# Revit family: Toilet-Round-American_Standard-Colony-221DB_Series
name_source: partatom
category: Plumbing Fixtures
units: mm (PartAtom-declared; Revit-internal decimal feet)

## family parameters
Always vertical = No
Cut with Voids When Loaded = No
OmniClass Number = 23.45.05.21.11.11
OmniClass Title = Water Operated Water Closets
Part Type = Normal
Room Calculation Point = No
Round Connector Dimension = Use Radius
Shared = Yes
Work Plane-Based = Yes

## types (3) — shared parameters
3251D.101 - Round Front Bowl = Yes
4192B.104 - Tank complete with trip lever located on left side = Yes
4192B.105 - Tank complete with trip lever located on right side = No
5322.011 - Rise and Shine solid plastic closed front round seat with cover = No
Assembly Code = D2010110
Bowl Shape = Round
CW Connection = Yes
CWFU = 5
Cold Water Connection Diameter = 3/8"
Cold Water Connection Height = 10"
Cold Water Connection Radius = 3/16"
Cold Water Connection Width = 6"
Default Elevation = 0"
Description = Colony® Two-Piece 1.28 gpf/4.8 Lpf Standard Height Round Front 10-Inch Rough Toilet Less Seat
Flush Rate = 1.28Gpf (4.8Lpf)
HW Connection = No
Height = 29 1/2"
IAPMO Compliance = ASME A112.19.2-2008/CSA B45.1-08 for Vitreous China Fixtures and US EPA WaterSense® Specification for HETs
Installation Type = Floor Mounted
Length = 25 13/16"
Manufacturer = American Standard
Price = Prices may vary. Please consult Manufacturer Representative for most up-to-date price list.
Product Documentation Link = https://americanstandard.box.com
Product Page URL = https://www.americanstandard-us.com
Revised Date = 07/20/2022
Type Comments = Available Finishes White, Bone, Linen
URL = http://www.americanstandard-us.com
Vent Connection = No
WFU = 5
Warranty Information = 2 Year Limited
Waste Connection = Yes
Waste Connection Diameter = 2"
Waste Connection Radius = 1"
Width = 18 11/16"
zero-valued in all types: HWFU

## per-type parameters (varying)
| type | Finish | Material |
| 221DB.104.020 | Vitreous China-American Standard-020-White | Vitreous China-American Standard-020-White |
| 221DB.104.021 | Vitreous China-American Standard-021-Bone | Vitreous China-American Standard-021-Bone |
| 221DB.104.222 | Vitreous China-American Standard-222-Linen | Vitreous China-American Standard-222-Linen |

note: column(s) folded — value = type name in every type: Model

## geometry (parser evidence)
native form markers: Sweep x2
no freeform markers — native parametric forms only
